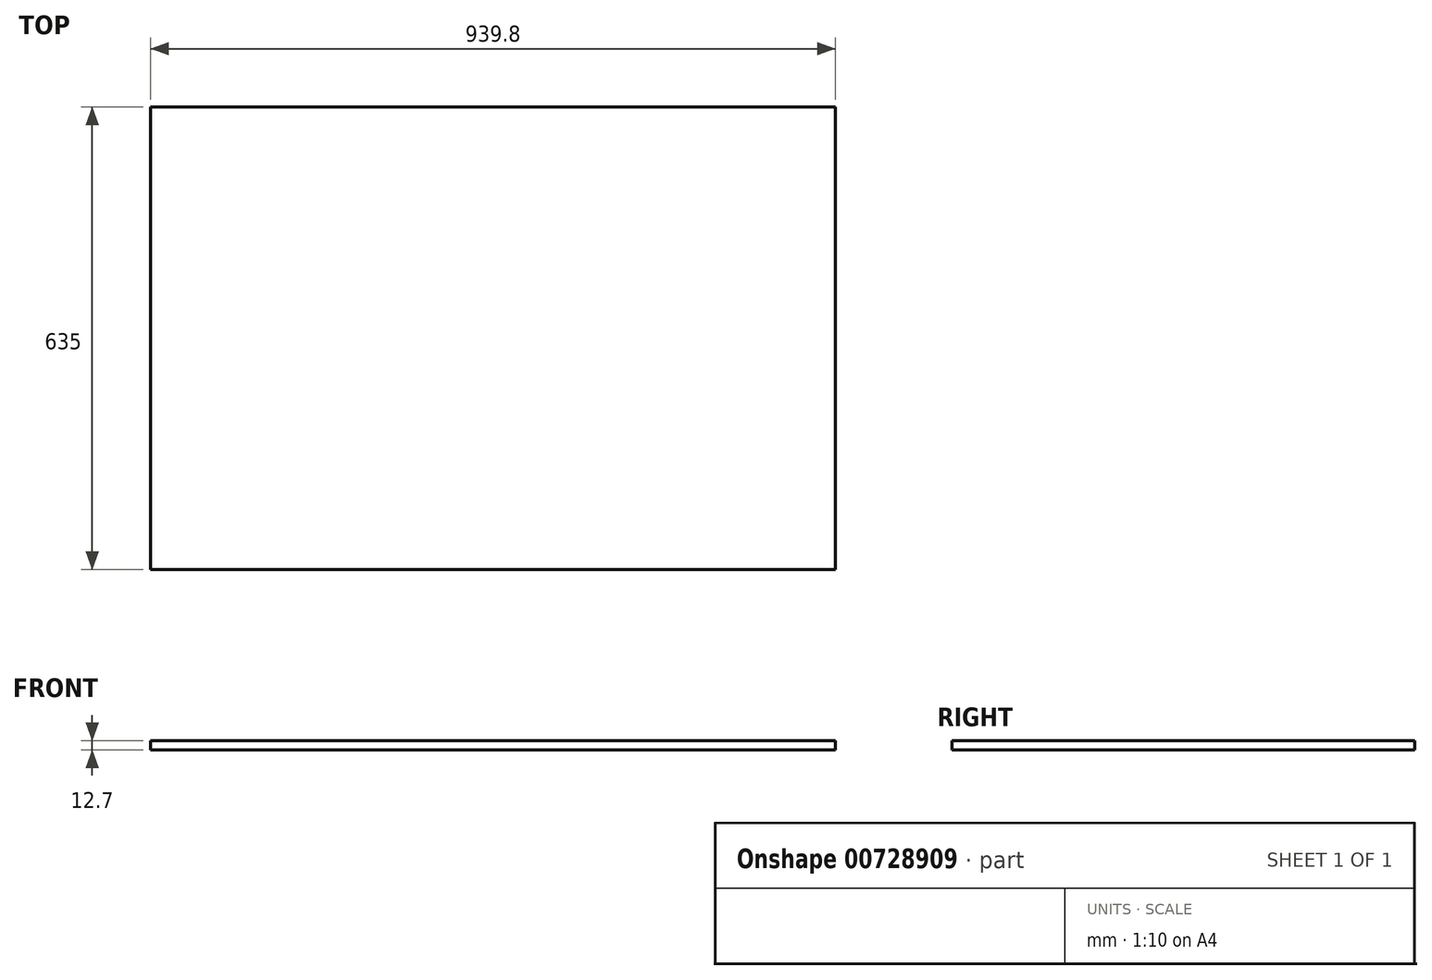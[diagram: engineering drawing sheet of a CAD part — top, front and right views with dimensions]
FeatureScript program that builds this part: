
annotation { "Feature Type Name" : "Feature", "Feature Type Description" : "" }
export const myFeature = defineFeature(function(context is Context, id is Id, definition is map)
    precondition{}
    {
        {
            var Q0;
            Q0=qCreatedBy(makeId("Top.planeOp"),FACE);
            var sketch = newSketch(context, id + "F0", { "sketchPlane" : qUnion([Q0])});
            skLineSegment(sketch, "E0.bottom", {"start": v(469.9, 317.5) * mm, "end": v(-469.9, 317.5) * mm});
            skLineSegment(sketch, "E0.top", {"start": v(469.9, -317.5) * mm, "end": v(-469.9, -317.5) * mm});
            skLineSegment(sketch, "E0.left", {"start": v(469.9, 317.5) * mm, "end": v(469.9, -317.5) * mm});
            skLineSegment(sketch, "E0.right", {"start": v(-469.9, 317.5) * mm, "end": v(-469.9, -317.5) * mm});
            skPoint(sketch, "E0.middle", {"position": v(0, 0) * mm});
            skSolve(sketch);
        }
        {
            var Q0;
            Q0=makeQuery(id+"F0.imprint","IMPRINT",FACE,{"disambiguationData":[TD([[makeQuery(id+"F0.imprint","IMPRINT",EDGE,{"derivedFrom":sQuery(id+"F0.wireOp",EDGE,"E0.bottom")}),1.0]])]});
            extrude(context, id + "F1", {"entities" : qUnion([Q0]), "oppositeDirection" : true, "depth" : 12.7 * mm, "offsetDistance" : 25.4 * mm});
        }
    });
